# Revit family: P191568KX-137c_KDPM604K
name_source: partatom
category: Specialty Equipment
units: mm (PartAtom-declared; Revit-internal decimal feet)

## family parameters
Always vertical = Yes
Cut with Voids When Loaded = No
Enable Cutting in Views = No
Maintain Annotation Orientation = No
Part Type = Normal
Room Calculation Point = No
Round Connector Dimension = Use Diameter
Shared = No
Work Plane-Based = No

## types (2) — shared parameters
Accent Material = ARCAT - Metal - Steel - Black
Amps = 0 A
Blanket Material = ARCAT - Fabric - Grey
Body Material = ARCAT - Metal - Plastic - Grey
Bottom Panel Material = ARCAT - Metal - Steel - Black Stainless
Clearance Material = ARCAT - Clearance
Default Elevation = 0"
Depth = 24 1/2"
Display Panel Material = ARCAT - Glass - Black
Family Name = DISH
Handle Material = ARCAT - Plastic - Grey
Height = 33 1/2"
Manufacturer = KitchenAid
Voltage = 0 V
Width = 23 7/8"

## per-type parameters (varying)
| type | Door Material |
| KDPM604KPS | ARCAT - Metal - Steel - Stainless |
| KDPM604KBS | ARCAT - Metal - Steel - Black Stainless |

note: column(s) folded — value = type name in every type: Model

## geometry (parser evidence)
native form markers: Sweep x1
no freeform markers — native parametric forms only
